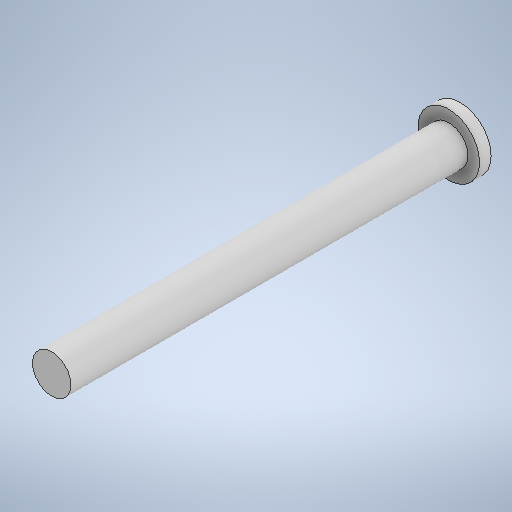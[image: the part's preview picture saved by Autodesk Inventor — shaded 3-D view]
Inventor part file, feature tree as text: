
AUTODESK INVENTOR PART (.ipt)
format: ipt  version: 2025.1 (Build 291241020, 241B)  size: 254,464 bytes
history: native  units: mm
features: extrude x2, sketch x2
ambient origin geometry x8: Origin, YZ Plane, XZ Plane, XY Plane, X Axis, Y Axis, Z Axis, Center Point
bodies: Solid1 (feature_tree)
feature tree (4):
  extrude  "Extrusion1"  Depth=103.0mm TaperAngle=0.0deg
  extrude  "Extrusion2"  Depth=3.0mm TaperAngle=0.0deg
  sketch  "Sketch1"  dims[d0=10.0mm d1=103.0mm d2=0.0mm]
  sketch  "Sketch2"  dims[d3=16.0mm d4=3.0mm d5=0.0mm]
